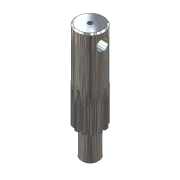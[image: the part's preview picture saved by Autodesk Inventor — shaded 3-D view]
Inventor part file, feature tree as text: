
AUTODESK INVENTOR PART (.ipt)
format: ipt  version: unknown  size: 824,320 bytes
history: native  units: mm (DEFAULTED — no unit token found)
features: sketch x17, projected_geometry x16, revolve x12, other x4, extrude x4, chamfer x2, plane x2, pattern_circular x1, hole x1
ambient origin geometry x5: Origin, X Axis, Y Axis, Z Axis, Center Point
feature tree (59):
  other  "Embedding 1"
  extrude  "Extrusion1"  Depth=2.116667mm
  pattern_circular  "Circular Pattern1"  Count=12  [1 undecoded]
  extrude  "Extrusion2"  Depth=29.758mm
  extrude  "Extrusion3"  Depth=18.9992mm
  chamfer  "Chamfer1"  Distance=30.1498mm
  chamfer  "Chamfer2"  Distance=1.5875mm
  plane  "Work Plane2"
  extrude  "Extrusion4"  Depth=16.75mm
  plane  "Work Plane3"
  revolve  "Revolution1"  [1 undecoded]
  revolve  "Revolution2"  [1 undecoded]
  revolve  "Revolution3"  [1 undecoded]
  sketch  "Sketch13"  dims[d8=0.498475mm]
  revolve  "Revolution5"  [1 undecoded]
  revolve  "Revolution6"  [1 undecoded]
  revolve  "Revolution7"  [1 undecoded]
  revolve  "Revolution8"  Angle=90.0deg
  revolve  "Revolution9"  Angle=90.0deg
  revolve  "Revolution10"  [1 undecoded]
  revolve  "Revolution11"  Angle=90.0deg
  revolve  "Revolution12"  Angle=90.0deg
  revolve  "Revolution13"  [1 undecoded]
  hole  "Hole1"  [1 undecoded]
  other  "RIGHT"
  other  "TOP"
  other  "FRONT"
  sketch  "Sketch1"  dims[d0=25.4mm d1=2.116667mm]
  sketch  "Sketch2"  dims[d2=3.490659mm]
  sketch  "Sketch3"  dims[d3=4.56565mm]
  sketch  "Sketch4"  dims[d4=6.7945mm]
  sketch  "Sketch10"  dims[d5=5.545667mm]
  projected_geometry  "Projected Loop2"
  projected_geometry  "Projected Loop3"
  projected_geometry  "Projected Loop4"
  projected_geometry  "Projected Loop5"
  sketch  "Sketch11"  dims[d6=1.308997mm]
  projected_geometry  "Projected Loop6"
  sketch  "Sketch12"  dims[d7=1.308997mm]
  projected_geometry  "Projected Loop7"
  projected_geometry  "Projected Loop8"
  sketch  "Sketch14"  dims[d9=25.4mm d10=0.0mm d11=120.0mm]
  projected_geometry  "Projected Loop9"
  sketch  "Sketch15"  dims[d13=360.0deg d14=29.758mm]
  projected_geometry  "Projected Loop10"
  sketch  "Sketch16"  dims[d15=71.4502mm d16=0.0mm d17=18.9992mm d18=30.1498mm d19=0.0mm d20=1.5875mm d21=2.0mm]
  projected_geometry  "Projected Loop11"
  sketch  "Sketch17"  dims[d22=1.5875mm d23=2.0mm d25=16.75mm]
  projected_geometry  "Projected Loop12"
  sketch  "Sketch18"  dims[d26=13.081mm d27=12.7mm]
  projected_geometry  "Projected Loop13"
  sketch  "Sketch19"  dims[d28=50.8mm d29=0.0mm d32=40.0mm]
  projected_geometry  "Projected Loop14"
  sketch  "Sketch20"  dims[d33=90.0deg d35=40.0mm]
  projected_geometry  "Projected Loop15"
  sketch  "Sketch21"  dims[d36=90.0deg d37=40.0mm]
  projected_geometry  "Projected Loop16"
  sketch  "Sketch22"  dims[d38=90.0deg d39=40.0mm d40=40.0mm d42=90.0deg d43=90.0deg d44=40.0mm d45=90.0deg d48=90.0deg d49=40.0mm d50=90.0deg d51=40.0mm d52=40.0mm d53=90.0deg d54=40.0mm d55=90.0deg d56=40.0mm d57=90.0deg d58=40.0mm d59=90.0deg d60=4.978mm d61=6.0mm d62=4.0mm d63=2.0mm d64=14.3117mm d65=8.0mm d66=20.594885mm d67=45.0deg d68=45.0deg]
  projected_geometry  "Projected Loop17"
note: 10 required parameter values undecoded (feature->parameter linkage not recoverable at this tier; creation-order binding heuristic only, values carry confidence <= 0.55)